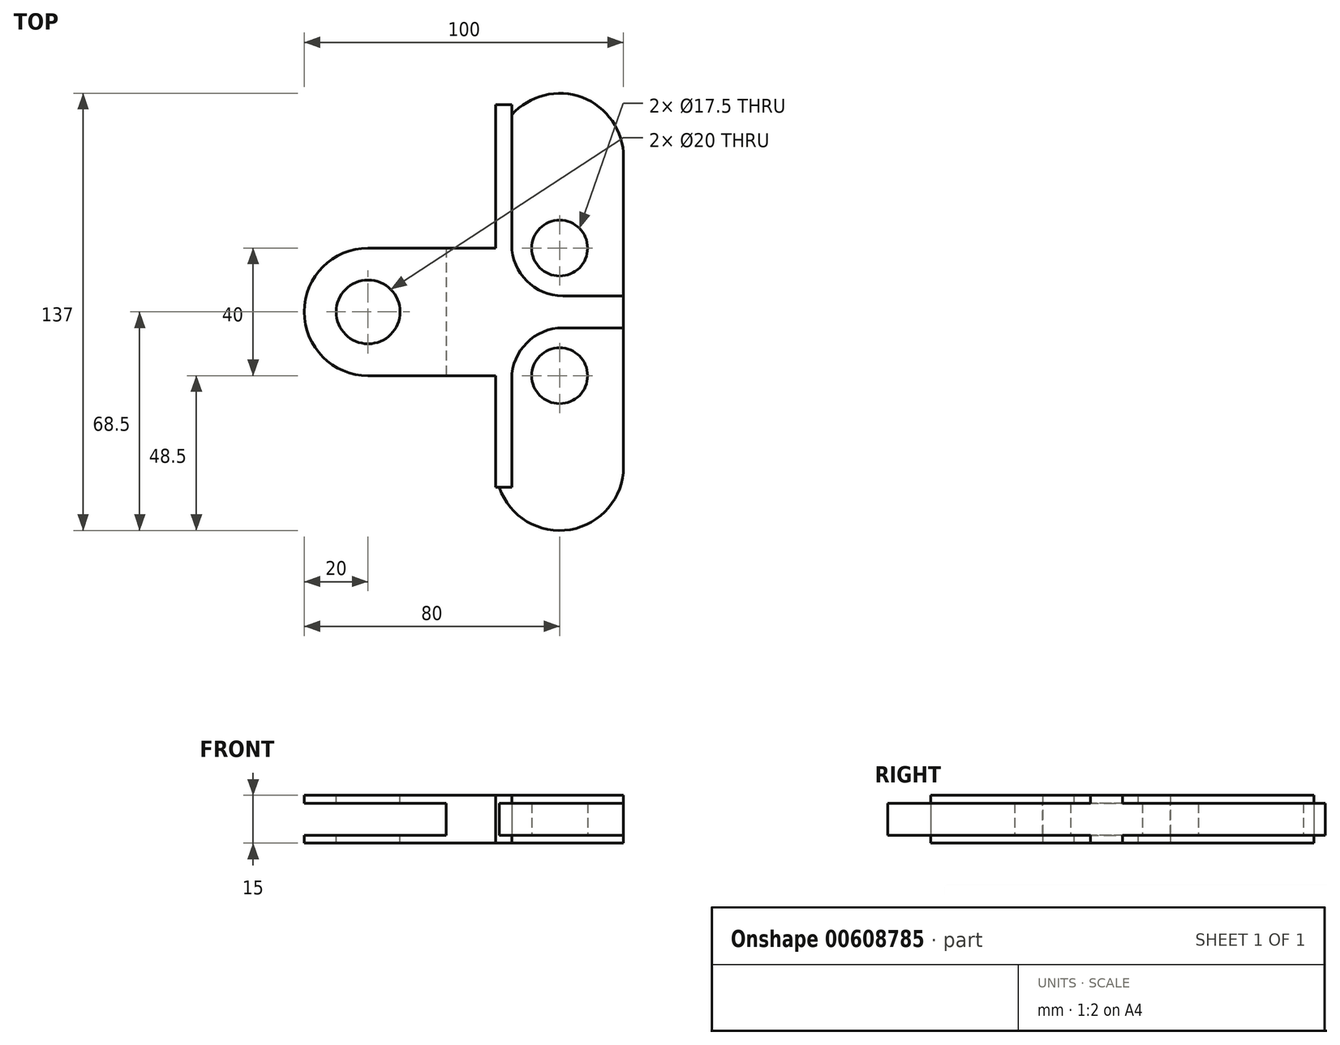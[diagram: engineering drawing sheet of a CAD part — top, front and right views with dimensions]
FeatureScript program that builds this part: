
annotation { "Feature Type Name" : "Feature", "Feature Type Description" : "" }
export const myFeature = defineFeature(function(context is Context, id is Id, definition is map)
    precondition{}
    {
        {
            var Q0;
            Q0=qCreatedBy(makeId("Top.planeOp"),FACE);
            var sketch = newSketch(context, id + "F0", { "sketchPlane" : qUnion([Q0])});
            skArc(sketch, "E0", {"start": v(20, 48.5) * mm, "mid": v(0, 68.5) * mm, "end": v(-20, 48.5) * mm});
            skArc(sketch, "E1", {"start": v(-20, -48.5) * mm, "mid": v(0, -68.5) * mm, "end": v(20, -48.5) * mm});
            skLineSegment(sketch, "E2", {"start": v(-20, 48.5) * mm, "end": v(-20, -48.5) * mm});
            skLineSegment(sketch, "E3", {"start": v(20, 48.5) * mm, "end": v(20, -48.5) * mm});
            skSolve(sketch);
        }
        {
            var Q0;
            Q0 = qSketchRegion(id + "F0", true);
            extrude(context, id + "F1", {"entities" : qUnion([Q0]), "depth" : 10 * mm, "offsetDistance" : 25 * mm, "symmetric" : true});
        }
        {
            var Q0;
            Q0=qCreatedBy(makeId("Top.planeOp"),FACE);
            var sketch = newSketch(context, id + "F2", { "sketchPlane" : qUnion([Q0])});
            skCircle(sketch, "E4", {"center": v(0, 20) * mm, "radius": 8.75 * mm});
            skCircle(sketch, "E5", {"center": v(0, -20) * mm, "radius": 8.75 * mm});
            skSolve(sketch);
        }
        {
            var Q0;
            Q0 = qSketchRegion(id + "F2", true);
            extrude(context, id + "F3", {"entities" : qUnion([Q0]), "operationType" : NewBodyOperationType.REMOVE, "flatOperationType" : FlatOperationType.REMOVE, "depth" : 25 * mm, "offsetDistance" : 25 * mm, "domain" : OperationDomain.MODEL, "symmetric" : true});
        }
        {
            var Q0;
            Q0=qCreatedBy(makeId("Top.planeOp"),FACE);
            var sketch = newSketch(context, id + "F4", { "sketchPlane" : qUnion([Q0])});
            skLineSegment(sketch, "E6.bottom", {"start": v(-20, 65) * mm, "end": v(-15, 65) * mm});
            skLineSegment(sketch, "E6.top", {"start": v(-20, -55) * mm, "end": v(-15, -55) * mm});
            skLineSegment(sketch, "E6.left", {"start": v(-20, 65) * mm, "end": v(-20, 20) * mm});
            skLineSegment(sketch, "E6.right", {"start": v(-15, 65) * mm, "end": v(-15, 21) * mm});
            skLineSegment(sketch, "E7.bottom", {"start": v(20, -5) * mm, "end": v(1, -5) * mm});
            skLineSegment(sketch, "E7.top", {"start": v(20, 5) * mm, "end": v(1, 5) * mm});
            skLineSegment(sketch, "E7.left", {"start": v(20, 5) * mm, "end": v(20, -5) * mm});
            skLineSegment(sketch, "E8.bottom", {"start": v(-60, 20) * mm, "end": v(-20, 20) * mm});
            skLineSegment(sketch, "E8.top", {"start": v(-60, -20) * mm, "end": v(-20, -20) * mm});
            skLineSegment(sketch, "E9.trimOffspring", {"start": v(-20, -20) * mm, "end": v(-20, -55) * mm});
            skLineSegment(sketch, "E10.trimOffspring", {"start": v(-15, -21) * mm, "end": v(-15, -55) * mm});
            skArc(sketch, "E11.filletArc", {"start": v(1, -5) * mm, "mid": v(-10.31, -9.69) * mm, "end": v(-15, -21) * mm});
            skPoint(sketch, "E12.visualSharp", {"position": v(-15, 5) * mm});
            skArc(sketch, "E12.filletArc", {"start": v(-15, 21) * mm, "mid": v(-10.31, 9.69) * mm, "end": v(1, 5) * mm});
            skArc(sketch, "E13", {"start": v(-60, 20) * mm, "mid": v(-80, 0) * mm, "end": v(-60, -20) * mm});
            skSolve(sketch);
        }
        {
            var Q0;
            Q0 = qSketchRegion(id + "F4", true);
            extrude(context, id + "F5", {"entities" : qUnion([Q0]), "operationType" : NewBodyOperationType.ADD, "depth" : 15 * mm, "offsetDistance" : 25 * mm, "symmetric" : true});
        }
        {
            var Q0;
            Q0=qCreatedBy(makeId("Top.planeOp"),FACE);
            var sketch = newSketch(context, id + "F6", { "sketchPlane" : qUnion([Q0])});
            skLineSegment(sketch, "E14.0", {"start": v(-60, 20) * mm, "end": v(-35.5, 20) * mm});
            skArc(sketch, "E15.0.0", {"start": v(-60, 20) * mm, "mid": v(-80, 0) * mm, "end": v(-60, -20) * mm});
            skArc(sketch, "E15.0.2", {"start": v(-60, -20) * mm, "mid": v(-80, 0) * mm, "end": v(-60, 20) * mm});
            skLineSegment(sketch, "E16.0.0", {"start": v(-60, -20) * mm, "end": v(-35.5, -20) * mm});
            skLineSegment(sketch, "E16.0.2", {"start": v(-35.5, -20) * mm, "end": v(-60, -20) * mm});
            skLineSegment(sketch, "E17", {"start": v(-35.5, 20) * mm, "end": v(-35.5, -20) * mm});
            skPoint(sketch, "E18.orphan", {"position": v(-20, -20) * mm});
            skPoint(sketch, "E19.orphan", {"position": v(-20, 20) * mm});
            skSolve(sketch);
        }
        {
            var Q0;
            Q0 = qSketchRegion(id + "F6", true);
            extrude(context, id + "F7", {"entities" : qUnion([Q0]), "operationType" : NewBodyOperationType.REMOVE, "oppositeDirection" : true, "depth" : 10 * mm, "offsetDistance" : 25 * mm, "symmetric" : true});
        }
        {
            var Q0;
            Q0=makeQuery(id+"F5.opExtrude","CAP_FACE",FACE,{"disambiguationData":[OSD([sQuery(id+"F4.wireOp",EDGE,"E6.bottom"),sQuery(id+"F4.wireOp",EDGE,"E6.top"),sQuery(id+"F4.wireOp",EDGE,"E6.left"),sQuery(id+"F4.wireOp",EDGE,"E6.right"),sQuery(id+"F4.wireOp",EDGE,"E7.bottom"),sQuery(id+"F4.wireOp",EDGE,"E7.top"),sQuery(id+"F4.wireOp",EDGE,"E7.left"),sQuery(id+"F4.wireOp",EDGE,"E8.bottom"),sQuery(id+"F4.wireOp",EDGE,"E8.top"),sQuery(id+"F4.wireOp",EDGE,"E9.trimOffspring"),sQuery(id+"F4.wireOp",EDGE,"E10.trimOffspring"),sQuery(id+"F4.wireOp",EDGE,"E11.filletArc"),sQuery(id+"F4.wireOp",EDGE,"E12.filletArc"),sQuery(id+"F4.wireOp",EDGE,"E13")])],"isStart":false});
            var sketch = newSketch(context, id + "F8", { "sketchPlane" : qUnion([Q0])});
            skCircle(sketch, "E20", {"center": v(-60, 0) * mm, "radius": 10 * mm});
            skSolve(sketch);
        }
        {
            var Q0;
            Q0 = qSketchRegion(id + "F8", true);
            extrude(context, id + "F9", {"entities" : qUnion([Q0]), "operationType" : NewBodyOperationType.REMOVE, "oppositeDirection" : true, "depth" : 25 * mm, "offsetDistance" : 25 * mm});
        }
    });
